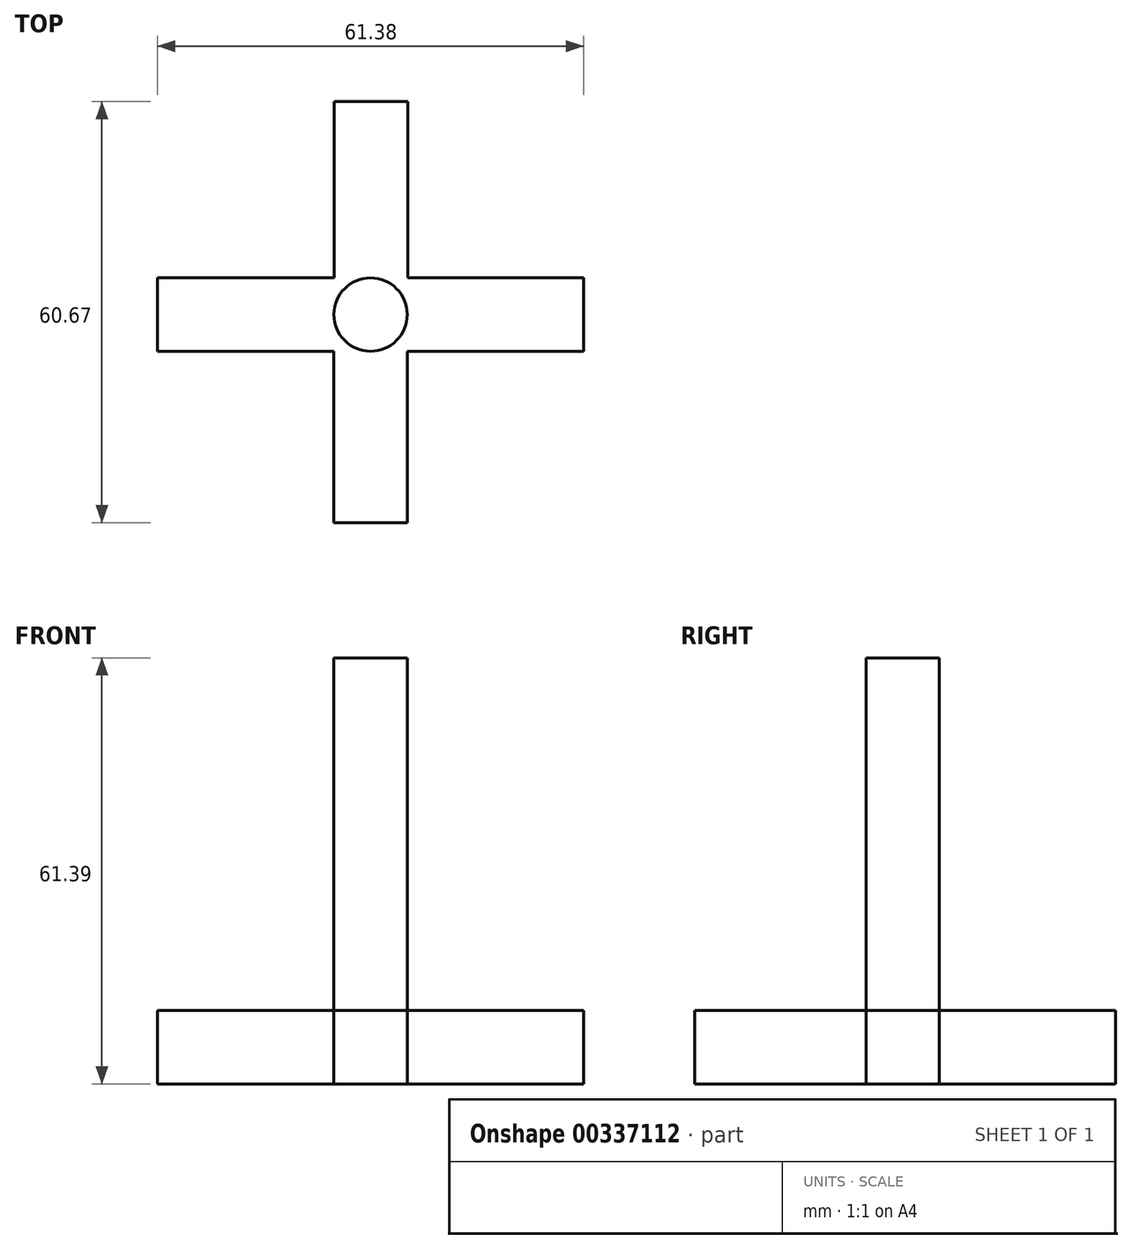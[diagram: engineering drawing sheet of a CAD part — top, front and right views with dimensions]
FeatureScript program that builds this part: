
annotation { "Feature Type Name" : "Feature", "Feature Type Description" : "" }
export const myFeature = defineFeature(function(context is Context, id is Id, definition is map)
    precondition{}
    {
        {
            var Q0;
            Q0=qCreatedBy(makeId("Top.planeOp"),FACE);
            var sketch = newSketch(context, id + "F0", { "sketchPlane" : qUnion([Q0])});
            skCircle(sketch, "E0", {"center": v(0, 0) * mm, "radius": 5.3 * mm});
            skSolve(sketch);
        }
        {
            var Q0;
            Q0 = qSketchRegion(id + "F0", true);
            extrude(context, id + "F1", {"entities" : qUnion([Q0]), "depth" : 50.8 * mm});
        }
        {
            var Q0;
            Q0=qCreatedBy(makeId("Front.planeOp"),FACE);
            var sketch = newSketch(context, id + "F2", { "sketchPlane" : qUnion([Q0])});
            skLineSegment(sketch, "E1.bottom", {"start": v(30.7, 0) * mm, "end": v(-30.7, 0) * mm});
            skLineSegment(sketch, "E1.top", {"start": v(30.7, -10.58) * mm, "end": v(-30.7, -10.58) * mm});
            skLineSegment(sketch, "E1.left", {"start": v(30.7, 0) * mm, "end": v(30.7, -10.58) * mm});
            skLineSegment(sketch, "E1.right", {"start": v(-30.7, 0) * mm, "end": v(-30.7, -10.58) * mm});
            skPoint(sketch, "E1.middle", {"position": v(0, -5.3) * mm});
            skSolve(sketch);
        }
        {
            var Q0;
            Q0=makeQuery(id+"F2.imprint","IMPRINT",FACE,{"disambiguationData":[TD([[makeQuery(id+"F2.imprint","IMPRINT",EDGE,{"derivedFrom":sQuery(id+"F2.wireOp",EDGE,"E1.bottom")}),1.0]])]});
            extrude(context, id + "F3", {"entities" : qUnion([Q0]), "operationType" : NewBodyOperationType.ADD, "depth" : 5.28 * mm});
        }
        {
            var Q0;
            Q0=makeQuery(id+"F3.opExtrude","CAP_FACE",FACE,{"disambiguationData":[OSD([sQuery(id+"F2.wireOp",EDGE,"E1.bottom"),sQuery(id+"F2.wireOp",EDGE,"E1.top"),sQuery(id+"F2.wireOp",EDGE,"E1.left"),sQuery(id+"F2.wireOp",EDGE,"E1.right")])],"isStart":true});
            extrude(context, id + "F4", {"entities" : qUnion([Q0]), "operationType" : NewBodyOperationType.ADD, "depth" : 5.28 * mm});
        }
        {
            var Q0;
            Q0=qCreatedBy(makeId("Right.planeOp"),FACE);
            var sketch = newSketch(context, id + "F5", { "sketchPlane" : qUnion([Q0])});
            skLineSegment(sketch, "E2.bottom", {"start": v(-4.6, 0) * mm, "end": v(-30, 0) * mm});
            skLineSegment(sketch, "E2.top", {"start": v(-4.6, -10.58) * mm, "end": v(-30, -10.58) * mm});
            skLineSegment(sketch, "E2.left", {"start": v(-4.6, 0) * mm, "end": v(-4.6, -10.58) * mm});
            skLineSegment(sketch, "E2.right", {"start": v(-30, 0) * mm, "end": v(-30, -10.58) * mm});
            skSolve(sketch);
        }
        {
            var Q0;
            Q0=makeQuery(id+"F5.imprint","IMPRINT",FACE,{"disambiguationData":[TD([[makeQuery(id+"F5.imprint","IMPRINT",EDGE,{"derivedFrom":sQuery(id+"F5.wireOp",EDGE,"E2.bottom")}),1.0]])]});
            extrude(context, id + "F6", {"entities" : qUnion([Q0]), "operationType" : NewBodyOperationType.ADD, "depth" : 5.28 * mm});
        }
        {
            var Q0;
            Q0=makeQuery(id+"F6.opExtrude","CAP_FACE",FACE,{"disambiguationData":[OSD([sQuery(id+"F5.wireOp",EDGE,"E2.bottom"),sQuery(id+"F5.wireOp",EDGE,"E2.top"),sQuery(id+"F5.wireOp",EDGE,"E2.left"),sQuery(id+"F5.wireOp",EDGE,"E2.right")])],"isStart":true});
            extrude(context, id + "F7", {"entities" : qUnion([Q0]), "operationType" : NewBodyOperationType.ADD, "depth" : 5.28 * mm});
        }
        {
            var Q0;
            Q0=qCreatedBy(makeId("Right.planeOp"),FACE);
            var sketch = newSketch(context, id + "F8", { "sketchPlane" : qUnion([Q0])});
            skLineSegment(sketch, "E3.bottom", {"start": v(5.3, 0) * mm, "end": v(30.7, 0) * mm});
            skLineSegment(sketch, "E3.top", {"start": v(5.3, -10.6) * mm, "end": v(30.7, -10.6) * mm});
            skLineSegment(sketch, "E3.left", {"start": v(5.3, 0) * mm, "end": v(5.3, -10.6) * mm});
            skLineSegment(sketch, "E3.right", {"start": v(30.7, 0) * mm, "end": v(30.7, -10.6) * mm});
            skSolve(sketch);
        }
        {
            var Q0;
            Q0 = qSketchRegion(id + "F8", true);
            extrude(context, id + "F9", {"entities" : qUnion([Q0]), "depth" : 5.28 * mm});
        }
        {
            var Q0;
            Q0=makeQuery(id+"F9.opExtrude","CAP_FACE",FACE,{"disambiguationData":[OSD([sQuery(id+"F8.wireOp",EDGE,"E3.bottom"),sQuery(id+"F8.wireOp",EDGE,"E3.top"),sQuery(id+"F8.wireOp",EDGE,"E3.left"),sQuery(id+"F8.wireOp",EDGE,"E3.right")])],"isStart":true});
            extrude(context, id + "F10", {"entities" : qUnion([Q0]), "operationType" : NewBodyOperationType.ADD, "depth" : 5.28 * mm});
        }
        {
            var Q0;
            Q0=makeQuery(id+"F9.opExtrude","SWEPT_BODY",BODY,{"disambiguationData":[OSD([sQuery(id+"F8.wireOp",EDGE,"E3.bottom"),sQuery(id+"F8.wireOp",EDGE,"E3.top"),sQuery(id+"F8.wireOp",EDGE,"E3.left"),sQuery(id+"F8.wireOp",EDGE,"E3.right")])]});
            deleteBodies(context, id + "F11", {"entities" : qUnion([Q0])});
        }
        {
            var Q0;
            Q0=qCreatedBy(makeId("Front.planeOp"),FACE);
            var sketch = newSketch(context, id + "F12", { "sketchPlane" : qUnion([Q0])});
            skLineSegment(sketch, "E4.bottom", {"start": v(5.37, 0) * mm, "end": v(-5.22, 0) * mm});
            skLineSegment(sketch, "E4.top", {"start": v(5.37, -10.6) * mm, "end": v(-5.22, -10.6) * mm});
            skLineSegment(sketch, "E4.left", {"start": v(5.37, 0) * mm, "end": v(5.37, -10.6) * mm});
            skLineSegment(sketch, "E4.right", {"start": v(-5.22, 0) * mm, "end": v(-5.22, -10.6) * mm});
            skSolve(sketch);
        }
        {
            var Q0;
            Q0 = qSketchRegion(id + "F12", true);
            extrude(context, id + "F13", {"entities" : qUnion([Q0]), "operationType" : NewBodyOperationType.ADD, "oppositeDirection" : true, "depth" : 30.68 * mm});
        }
    });
